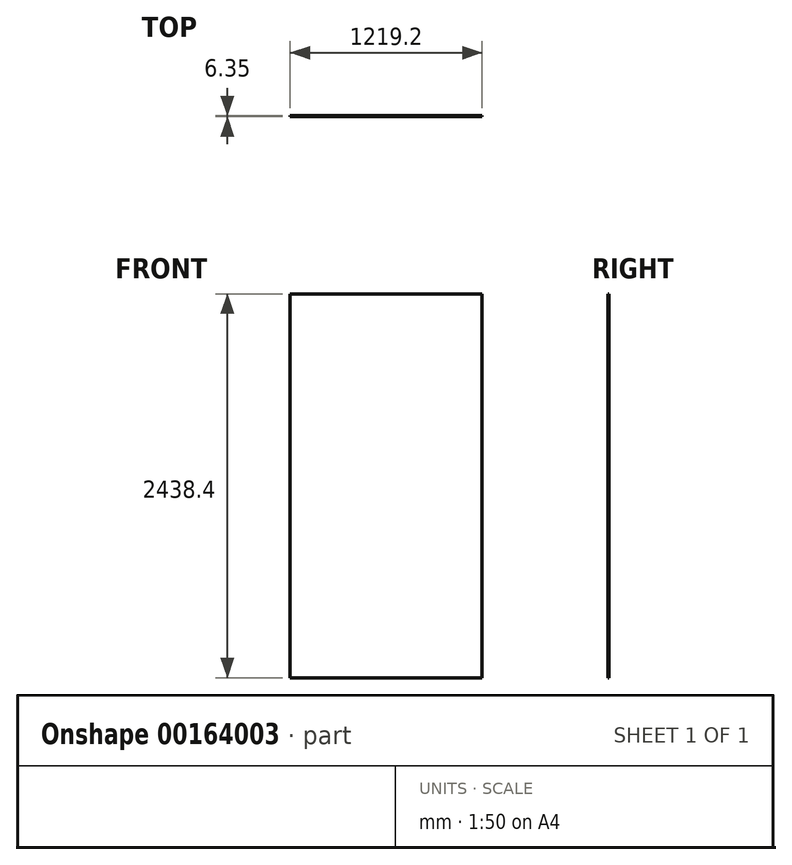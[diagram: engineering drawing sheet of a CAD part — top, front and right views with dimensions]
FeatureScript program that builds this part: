
annotation { "Feature Type Name" : "Feature", "Feature Type Description" : "" }
export const myFeature = defineFeature(function(context is Context, id is Id, definition is map)
    precondition{}
    {
        {
            var Q0;
            Q0=qCreatedBy(makeId("Front.planeOp"),FACE);
            var sketch = newSketch(context, id + "F0", { "sketchPlane" : qUnion([Q0])});
            skLineSegment(sketch, "E0.bottom", {"start": v(0, 0) * mm, "end": v(1219.2, 0) * mm});
            skLineSegment(sketch, "E0.top", {"start": v(0, 2438.4) * mm, "end": v(1219.2, 2438.4) * mm});
            skLineSegment(sketch, "E0.left", {"start": v(0, 0) * mm, "end": v(0, 2438.4) * mm});
            skLineSegment(sketch, "E0.right", {"start": v(1219.2, 0) * mm, "end": v(1219.2, 2438.4) * mm});
            skSolve(sketch);
        }
        {
            var Q0;
            Q0=makeQuery(id+"F0.imprint","IMPRINT",FACE,{"disambiguationData":[TD([[makeQuery(id+"F0.imprint","IMPRINT",EDGE,{"derivedFrom":sQuery(id+"F0.wireOp",EDGE,"E0.bottom")}),1.0]])]});
            extrude(context, id + "F1", {"entities" : qUnion([Q0]), "depth" : 6.35 * mm});
        }
    });
